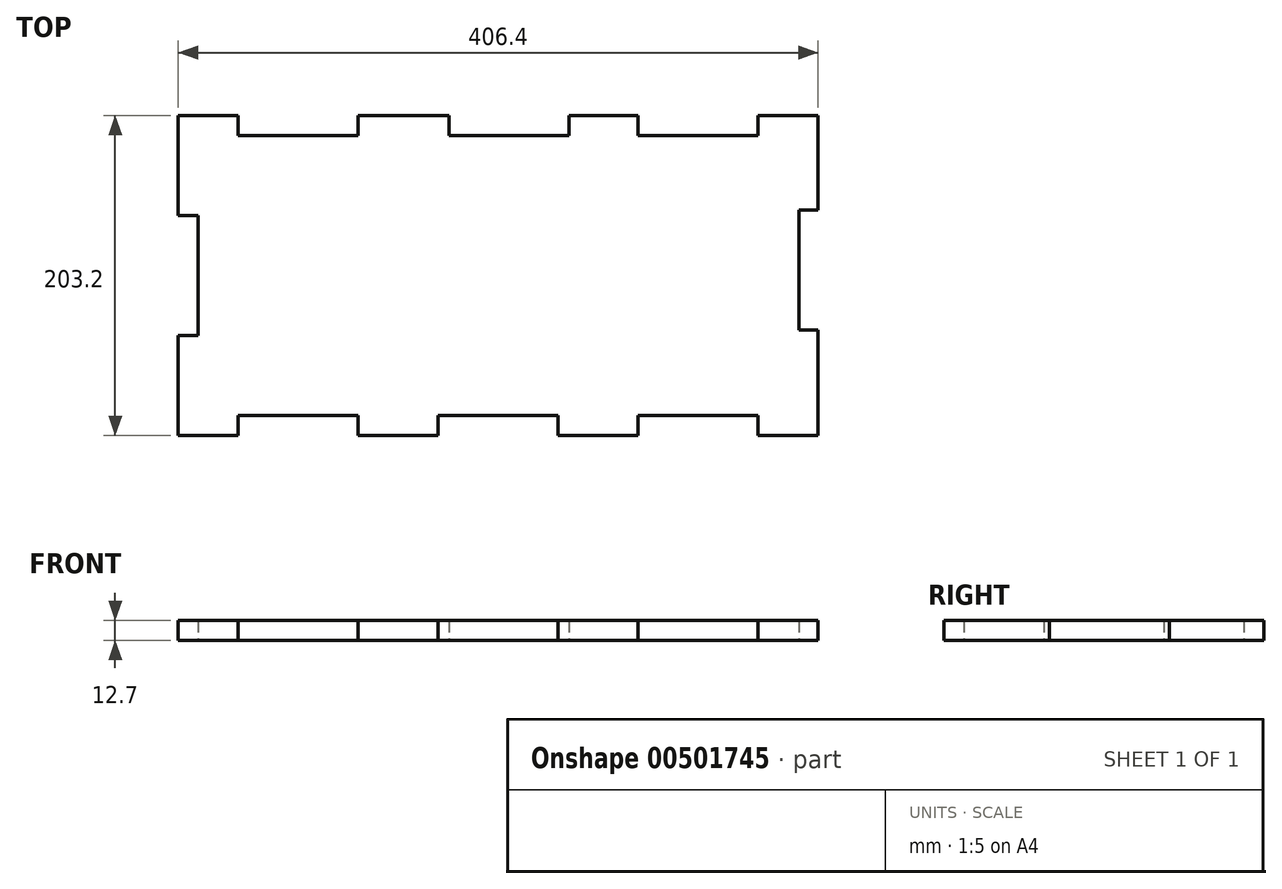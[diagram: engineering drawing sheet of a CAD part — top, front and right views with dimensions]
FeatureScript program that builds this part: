
annotation { "Feature Type Name" : "Feature", "Feature Type Description" : "" }
export const myFeature = defineFeature(function(context is Context, id is Id, definition is map)
    precondition{}
    {
        {
            var Q0;
            Q0=qCreatedBy(makeId("Top.planeOp"),FACE);
            var sketch = newSketch(context, id + "F0", { "sketchPlane" : qUnion([Q0])});
            skLineSegment(sketch, "E0.bottom", {"start": v(-203.2, 101.6) * mm, "end": v(203.2, 101.6) * mm});
            skLineSegment(sketch, "E0.top", {"start": v(-203.2, -101.6) * mm, "end": v(203.2, -101.6) * mm});
            skLineSegment(sketch, "E0.left", {"start": v(-203.2, 101.6) * mm, "end": v(-203.2, -101.6) * mm});
            skLineSegment(sketch, "E0.right", {"start": v(203.2, 101.6) * mm, "end": v(203.2, -101.6) * mm});
            skPoint(sketch, "E0.middle", {"position": v(0, 0) * mm});
            skLineSegment(sketch, "E1.top", {"start": v(-31.27, 88.9) * mm, "end": v(44.93, 88.9) * mm});
            skLineSegment(sketch, "E1.left", {"start": v(-31.27, 101.6) * mm, "end": v(-31.27, 88.9) * mm});
            skLineSegment(sketch, "E1.right", {"start": v(44.93, 101.6) * mm, "end": v(44.93, 88.9) * mm});
            skPoint(sketch, "E2.middle", {"position": v(-203.2, 0) * mm});
            skLineSegment(sketch, "E3.bottom", {"start": v(-203.2, 38.1) * mm, "end": v(-190.5, 38.1) * mm});
            skLineSegment(sketch, "E3.top", {"start": v(-203.2, -38.1) * mm, "end": v(-190.5, -38.1) * mm});
            skLineSegment(sketch, "E3.right", {"start": v(-190.5, 38.1) * mm, "end": v(-190.5, -38.1) * mm});
            skPoint(sketch, "E3.middle", {"position": v(-196.85, 0) * mm});
            skLineSegment(sketch, "E4.bottom", {"start": v(-38.1, -101.6) * mm, "end": v(38.1, -101.6) * mm});
            skLineSegment(sketch, "E4.top", {"start": v(-38.1, -88.9) * mm, "end": v(38.1, -88.9) * mm});
            skLineSegment(sketch, "E4.left", {"start": v(-38.1, -101.6) * mm, "end": v(-38.1, -88.9) * mm});
            skLineSegment(sketch, "E4.right", {"start": v(38.1, -101.6) * mm, "end": v(38.1, -88.9) * mm});
            skPoint(sketch, "E4.middle", {"position": v(0, -95.25) * mm});
            skPoint(sketch, "E5.middle.positionSnap0", {"position": v(203.2, 0) * mm});
            skPoint(sketch, "E5.centerSnap0", {"position": v(203.2, 0) * mm});
            skLineSegment(sketch, "E6.bottom", {"start": v(191.08, 41.62) * mm, "end": v(203.78, 41.62) * mm});
            skLineSegment(sketch, "E6.top", {"start": v(191.08, -34.58) * mm, "end": v(203.78, -34.58) * mm});
            skLineSegment(sketch, "E6.left", {"start": v(191.08, 41.62) * mm, "end": v(191.08, -34.58) * mm});
            skLineSegment(sketch, "E6.right", {"start": v(203.78, 41.62) * mm, "end": v(203.78, -34.58) * mm});
            skPoint(sketch, "E6.middle", {"position": v(191.08, 0) * mm});
            skLineSegment(sketch, "E7.bottom", {"start": v(-165.1, -101.6) * mm, "end": v(-88.9, -101.6) * mm});
            skLineSegment(sketch, "E7.top", {"start": v(-165.1, -88.9) * mm, "end": v(-88.9, -88.9) * mm});
            skLineSegment(sketch, "E7.left", {"start": v(-165.1, -101.6) * mm, "end": v(-165.1, -88.9) * mm});
            skLineSegment(sketch, "E7.right", {"start": v(-88.9, -101.6) * mm, "end": v(-88.9, -88.9) * mm});
            skLineSegment(sketch, "E8.bottom", {"start": v(165.1, -101.6) * mm, "end": v(88.9, -101.6) * mm});
            skLineSegment(sketch, "E8.top", {"start": v(165.1, -88.9) * mm, "end": v(88.9, -88.9) * mm});
            skLineSegment(sketch, "E8.left", {"start": v(165.1, -101.6) * mm, "end": v(165.1, -88.9) * mm});
            skLineSegment(sketch, "E8.right", {"start": v(88.9, -101.6) * mm, "end": v(88.9, -88.9) * mm});
            skLineSegment(sketch, "E9.bottom", {"start": v(165.1, 101.6) * mm, "end": v(88.9, 101.6) * mm});
            skLineSegment(sketch, "E9.top", {"start": v(165.1, 88.9) * mm, "end": v(88.9, 88.9) * mm});
            skLineSegment(sketch, "E9.left", {"start": v(165.1, 101.6) * mm, "end": v(165.1, 88.9) * mm});
            skLineSegment(sketch, "E9.right", {"start": v(88.9, 101.6) * mm, "end": v(88.9, 88.9) * mm});
            skLineSegment(sketch, "E10", {"start": v(-88.9, -88.9) * mm, "end": v(-88.9, 88.9) * mm, "construction": true});
            skLineSegment(sketch, "E11", {"start": v(-165.1, -88.9) * mm, "end": v(-165.1, 88.9) * mm, "construction": true});
            skLineSegment(sketch, "E12.bottom", {"start": v(-88.9, 88.9) * mm, "end": v(-165.1, 88.9) * mm});
            skLineSegment(sketch, "E12.top", {"start": v(-88.9, 101.6) * mm, "end": v(-165.1, 101.6) * mm});
            skLineSegment(sketch, "E12.left", {"start": v(-88.9, 88.9) * mm, "end": v(-88.9, 101.6) * mm});
            skLineSegment(sketch, "E12.right", {"start": v(-165.1, 88.9) * mm, "end": v(-165.1, 101.6) * mm});
            skSolve(sketch);
        }
        {
            var Q0;
            Q0=makeQuery(id+"F0.imprint","IMPRINT",FACE,{"disambiguationData":[TD([[makeQuery(id+"F0.imprint","IMPRINT",EDGE,{"derivedFrom":sQuery(id+"F0.wireOp",EDGE,"E1.top")}),-1.0]])]});
            extrude(context, id + "F1", {"entities" : qUnion([Q0]), "depth" : 12.7 * mm, "offsetDistance" : 25.4 * mm});
        }
    });
